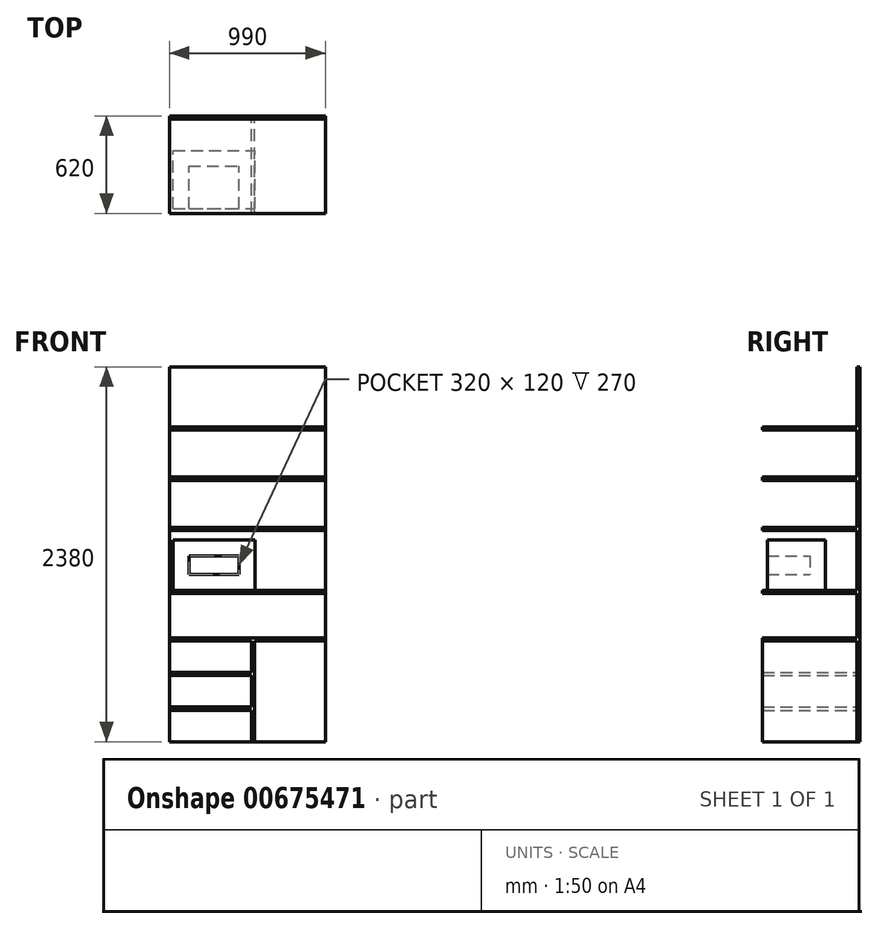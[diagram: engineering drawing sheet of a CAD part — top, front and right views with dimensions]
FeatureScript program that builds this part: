
annotation { "Feature Type Name" : "Feature", "Feature Type Description" : "" }
export const myFeature = defineFeature(function(context is Context, id is Id, definition is map)
    precondition{}
    {
        {
            var Q0;
            Q0=qCreatedBy(makeId("Front.planeOp"),FACE);
            var sketch = newSketch(context, id + "F0", { "sketchPlane" : qUnion([Q0])});
            skLineSegment(sketch, "E0.bottom", {"start": v(-495, 1190) * mm, "end": v(495, 1190) * mm});
            skLineSegment(sketch, "E0.top", {"start": v(-495, -1190) * mm, "end": v(495, -1190) * mm});
            skLineSegment(sketch, "E0.left", {"start": v(-495, 1190) * mm, "end": v(-495, -1190) * mm});
            skLineSegment(sketch, "E0.right", {"start": v(495, 1190) * mm, "end": v(495, -1190) * mm});
            skSolve(sketch);
        }
        {
            var Q0;
            Q0=makeQuery(id+"F0.imprint","IMPRINT",FACE,{"disambiguationData":[TD([[makeQuery(id+"F0.imprint","IMPRINT",EDGE,{"derivedFrom":sQuery(id+"F0.wireOp",EDGE,"E0.bottom")}),-1.0]])]});
            extrude(context, id + "F1", {"entities" : qUnion([Q0]), "depth" : 20 * mm, "offsetDistance" : 25.4 * mm});
        }
        {
            var Q0;
            Q0=makeQuery(id+"F1.opExtrude","CAP_FACE",FACE,{"disambiguationData":[OSD([sQuery(id+"F0.wireOp",EDGE,"E0.bottom"),sQuery(id+"F0.wireOp",EDGE,"E0.top"),sQuery(id+"F0.wireOp",EDGE,"E0.left"),sQuery(id+"F0.wireOp",EDGE,"E0.right")])],"isStart":false});
            var sketch = newSketch(context, id + "F2", { "sketchPlane" : qUnion([Q0])});
            skLineSegment(sketch, "E1.bottom", {"start": v(-495, -530) * mm, "end": v(495, -530) * mm});
            skLineSegment(sketch, "E1.top", {"start": v(-495, -550) * mm, "end": v(495, -550) * mm});
            skLineSegment(sketch, "E1.left", {"start": v(-495, -530) * mm, "end": v(-495, -550) * mm});
            skLineSegment(sketch, "E1.right", {"start": v(495, -530) * mm, "end": v(495, -550) * mm});
            skLineSegment(sketch, "E2.bottom", {"start": v(-495, -230) * mm, "end": v(495, -230) * mm});
            skLineSegment(sketch, "E2.top", {"start": v(-495, -250) * mm, "end": v(495, -250) * mm});
            skLineSegment(sketch, "E2.left", {"start": v(-495, -230) * mm, "end": v(-495, -250) * mm});
            skLineSegment(sketch, "E2.right", {"start": v(495, -230) * mm, "end": v(495, -250) * mm});
            skLineSegment(sketch, "E3.bottom", {"start": v(-495, 170) * mm, "end": v(495, 170) * mm});
            skLineSegment(sketch, "E3.top", {"start": v(-495, 150) * mm, "end": v(495, 150) * mm});
            skLineSegment(sketch, "E3.left", {"start": v(-495, 170) * mm, "end": v(-495, 150) * mm});
            skLineSegment(sketch, "E3.right", {"start": v(495, 170) * mm, "end": v(495, 150) * mm});
            skLineSegment(sketch, "E4.bottom", {"start": v(-495, 490) * mm, "end": v(495, 490) * mm});
            skLineSegment(sketch, "E4.top", {"start": v(-495, 470) * mm, "end": v(495, 470) * mm});
            skLineSegment(sketch, "E4.left", {"start": v(-495, 490) * mm, "end": v(-495, 470) * mm});
            skLineSegment(sketch, "E4.right", {"start": v(495, 490) * mm, "end": v(495, 470) * mm});
            skLineSegment(sketch, "E5.bottom", {"start": v(-495, 810) * mm, "end": v(495, 810) * mm});
            skLineSegment(sketch, "E5.top", {"start": v(-495, 790) * mm, "end": v(495, 790) * mm});
            skLineSegment(sketch, "E5.left", {"start": v(-495, 810) * mm, "end": v(-495, 790) * mm});
            skLineSegment(sketch, "E5.right", {"start": v(495, 810) * mm, "end": v(495, 790) * mm});
            skLineSegment(sketch, "E6.bottom", {"start": v(25, -550) * mm, "end": v(45, -550) * mm});
            skLineSegment(sketch, "E6.top", {"start": v(25, -1190) * mm, "end": v(45, -1190) * mm});
            skLineSegment(sketch, "E6.left", {"start": v(25, -550) * mm, "end": v(25, -1190) * mm});
            skLineSegment(sketch, "E6.right", {"start": v(45, -550) * mm, "end": v(45, -1190) * mm});
            skLineSegment(sketch, "E7.bottom", {"start": v(-495, -770) * mm, "end": v(25, -770) * mm});
            skLineSegment(sketch, "E7.top", {"start": v(-495, -750) * mm, "end": v(25, -750) * mm});
            skLineSegment(sketch, "E7.left", {"start": v(-495, -770) * mm, "end": v(-495, -750) * mm});
            skLineSegment(sketch, "E7.right", {"start": v(25, -770) * mm, "end": v(25, -750) * mm});
            skLineSegment(sketch, "E8.bottom", {"start": v(-495, -970) * mm, "end": v(25, -970) * mm});
            skLineSegment(sketch, "E8.top", {"start": v(-495, -990) * mm, "end": v(25, -990) * mm});
            skLineSegment(sketch, "E8.left", {"start": v(-495, -970) * mm, "end": v(-495, -990) * mm});
            skLineSegment(sketch, "E8.right", {"start": v(25, -970) * mm, "end": v(25, -990) * mm});
            skSolve(sketch);
        }
        {
            var Q0;
            Q0 = qSketchRegion(id + "F2", true);
            extrude(context, id + "F3", {"entities" : qUnion([Q0]), "operationType" : NewBodyOperationType.ADD, "depth" : 600 * mm, "offsetDistance" : 25 * mm});
        }
        {
            var Q0;
            {var subQ4=makeQuery(id+"F3.opExtrude","SWEPT_FACE",FACE,{"disambiguationData":[OSD([sQuery(id+"F2.wireOp",EDGE,"E2.bottom")])]});var subQ6=sQuery(id+"F0.wireOp",EDGE,"E0.left");var subQ7=makeQuery(id+"F1.opExtrude","SWEPT_FACE",FACE,{"disambiguationData":[OSD([subQ6])]});var subQ12=sQuery(id+"F0.wireOp",EDGE,"E0.right");Q0=makeQuery(id+"F6.boolean.opBoolean","SPLIT",FACE,{"disambiguationData":[TD([subQ7])],"derivedFrom":makeQuery(id+"F3.boolean.opBoolean","SPLIT",FACE,{"disambiguationData":[TD([subQ4])],"derivedFrom":makeQuery(id+"F1.opExtrude","CAP_FACE",FACE,{"disambiguationData":[OSD([sQuery(id+"F0.wireOp",EDGE,"E0.bottom"),sQuery(id+"F0.wireOp",EDGE,"E0.top"),subQ6,subQ12])],"isStart":false})})});}
            cPlane(context, id + "F4", {"entities" : qUnion([Q0]), "cplaneType" : CPlaneType.OFFSET, "offset" : 200 * mm, "width" : 150 * mm, "height" : 150 * mm});
        }
        {
            var Q0;
            Q0=qCreatedBy(id+"F4.planeOp",FACE);
            var sketch = newSketch(context, id + "F5", { "sketchPlane" : qUnion([Q0])});
            skLineSegment(sketch, "E9.bottom", {"start": v(-472.47, 91) * mm, "end": v(47.53, 91) * mm});
            skLineSegment(sketch, "E9.top", {"start": v(-472.47, -229) * mm, "end": v(47.53, -229) * mm});
            skLineSegment(sketch, "E9.left", {"start": v(-472.47, 91) * mm, "end": v(-472.47, -229) * mm});
            skLineSegment(sketch, "E9.right", {"start": v(47.53, 91) * mm, "end": v(47.53, -229) * mm});
            skSolve(sketch);
        }
        {
            var Q0;
            Q0=makeQuery(id+"F5.imprint","IMPRINT",FACE,{"disambiguationData":[TD([[makeQuery(id+"F5.imprint","IMPRINT",EDGE,{"derivedFrom":sQuery(id+"F5.wireOp",EDGE,"E9.bottom")}),-1.0]])]});
            extrude(context, id + "F6", {"entities" : qUnion([Q0]), "operationType" : NewBodyOperationType.ADD, "depth" : 370 * mm, "offsetDistance" : 25 * mm});
        }
        {
            var Q0;
            Q0=makeQuery(id+"F6.opExtrude","CAP_FACE",FACE,{"disambiguationData":[OSD([sQuery(id+"F5.wireOp",EDGE,"E9.bottom"),sQuery(id+"F5.wireOp",EDGE,"E9.top"),sQuery(id+"F5.wireOp",EDGE,"E9.left"),sQuery(id+"F5.wireOp",EDGE,"E9.right")])],"isStart":false});
            shell(context, id + "F7", {"entities" : qUnion([Q0]), "thickness" : 100 * mm});
        }
    });
